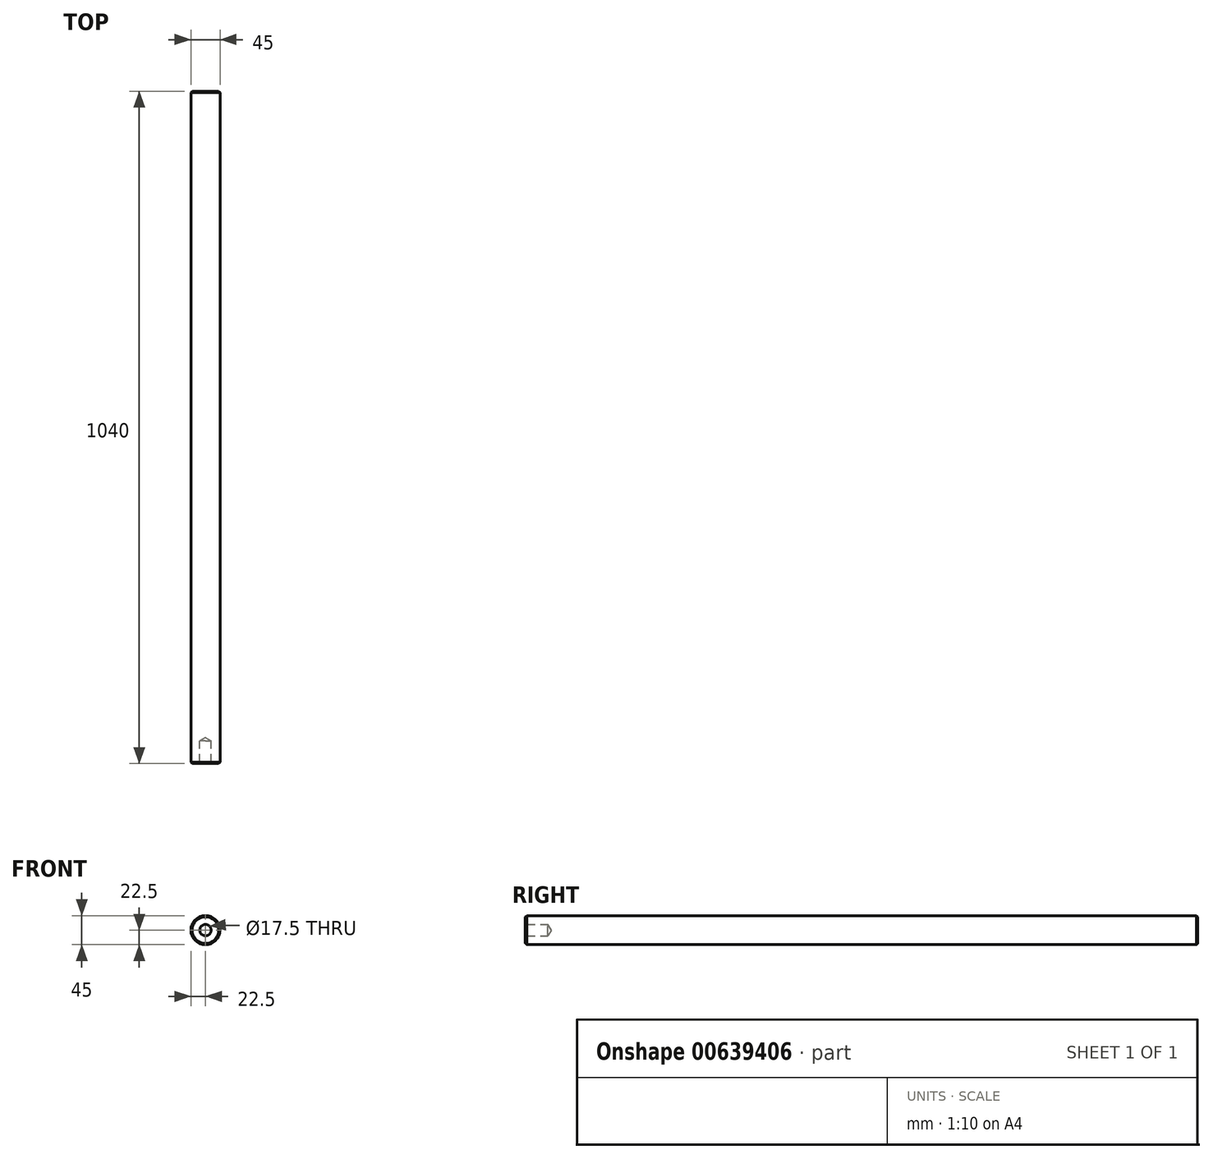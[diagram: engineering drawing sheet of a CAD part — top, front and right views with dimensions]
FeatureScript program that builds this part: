
annotation { "Feature Type Name" : "Feature", "Feature Type Description" : "" }
export const myFeature = defineFeature(function(context is Context, id is Id, definition is map)
    precondition{}
    {
        {
            var Q0;
            Q0=qCreatedBy(makeId("Front.planeOp"),FACE);
            var sketch = newSketch(context, id + "F0", { "sketchPlane" : qUnion([Q0])});
            skCircle(sketch, "E0", {"center": v(0, 0) * mm, "radius": 22.5 * mm});
            skSolve(sketch);
        }
        {
            var Q0;
            Q0=makeQuery(id+"F0.imprint","IMPRINT",FACE,{"disambiguationData":[TD([[makeQuery(id+"F0.imprint","IMPRINT",EDGE,{"derivedFrom":sQuery(id+"F0.wireOp",EDGE,"E0")}),1.0]])]});
            extrude(context, id + "F1", {"entities" : qUnion([Q0]), "depth" : 1040 * mm, "offsetDistance" : 25 * mm});
        }
        {
            var Q0;
            Q0=makeQuery(id+"F1.opExtrude","CAP_EDGE",EDGE,{"disambiguationData":[OSD([sQuery(id+"F0.wireOp",EDGE,"E0")])],"isStart":true});
            var Q1;
            Q1=makeQuery(id+"F1.opExtrude","CAP_EDGE",EDGE,{"disambiguationData":[OSD([sQuery(id+"F0.wireOp",EDGE,"E0")])],"isStart":false});
            chamfer(context, id + "F2", {"entities" : qUnion([Q0, Q1]), "width" : 2 * mm, "tangentPropagation" : true});
        }
        {
            var Q0;
            Q0=makeQuery(id+"F1.opExtrude","CAP_FACE",FACE,{"disambiguationData":[OSD([sQuery(id+"F0.wireOp",EDGE,"E0")])],"isStart":false});
            var sketch = newSketch(context, id + "F3", { "sketchPlane" : qUnion([Q0])});
            skPoint(sketch, "E1", {"position": v(0, 0) * mm});
            skSolve(sketch);
        }
        {
            var Q0;
            Q0=sQuery(id+"F3.wireOp",VERTEX,"E1");
            var Q1;
            Q1=makeQuery(id+"F1.opExtrude","SWEPT_BODY",BODY,{"disambiguationData":[OSD([sQuery(id+"F0.wireOp",EDGE,"E0")])]});
            hole(context, id + "F4", {"style" : HoleStyle.SIMPLE, "endStyle" : HoleEndStyle.BLIND, "standardTappedOrClearance" : lookupTablePath({ "standard" : "ISO", "engagement" : "75%", "pitch" : "2.5 mm", "size" : "M20", "type" : "Tapped" }), "standardBlindInLast" : lookupTablePath({ "standard" : "ISO", "engagement" : "75%", "pitch" : "2.5 mm", "size" : "M20", "type" : "Tapped" }), "holeDiameter" : 17.5 * mm, "majorDiameter" : 20 * mm, "showTappedDepth" : true, "holeDepth" : 35 * mm, "isTappedThrough" : true, "tappedDepth" : 30 * mm, "tapClearance" : 2, "locations" : qUnion([Q0]), "scope" : qUnion([Q1])});
        }
    });
